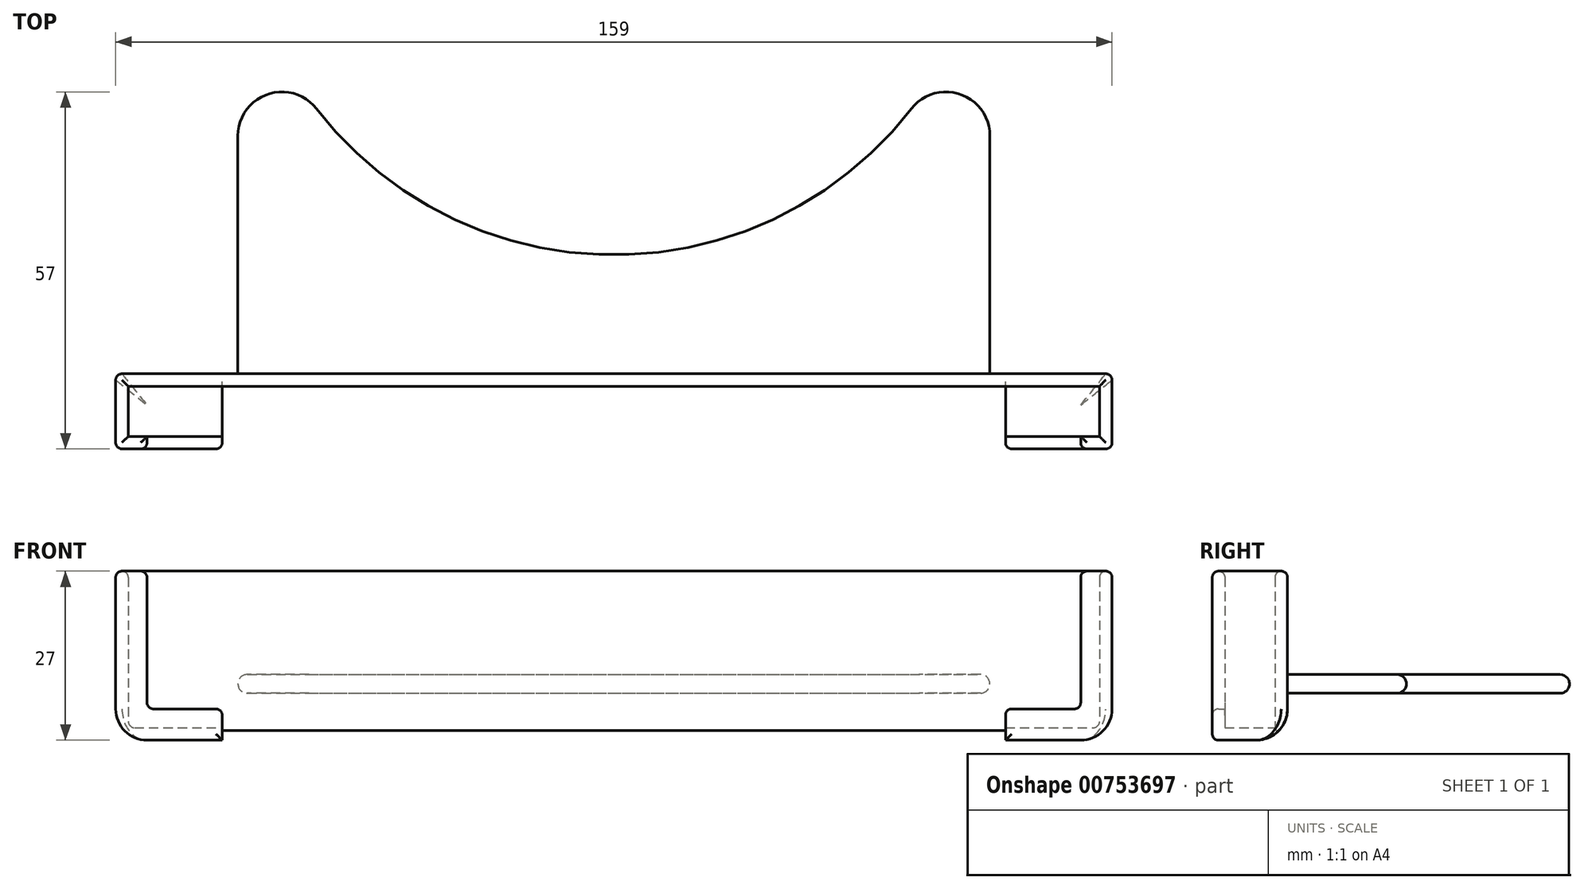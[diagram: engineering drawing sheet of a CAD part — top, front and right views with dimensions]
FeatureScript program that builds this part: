
annotation { "Feature Type Name" : "Feature", "Feature Type Description" : "" }
export const myFeature = defineFeature(function(context is Context, id is Id, definition is map)
    precondition{}
    {
        {
            var Q0;
            Q0=qCreatedBy(makeId("Front.planeOp"),FACE);
            var sketch = newSketch(context, id + "F0", { "sketchPlane" : qUnion([Q0])});
            skLineSegment(sketch, "E0.bottom", {"start": v(-77.5, 19.5) * mm, "end": v(77.5, 19.5) * mm});
            skLineSegment(sketch, "E0.top", {"start": v(-77.5, -5.5) * mm, "end": v(77.5, -5.5) * mm});
            skLineSegment(sketch, "E0.left", {"start": v(-77.5, 19.5) * mm, "end": v(-77.5, -5.5) * mm});
            skLineSegment(sketch, "E0.right", {"start": v(77.5, 19.5) * mm, "end": v(77.5, -5.5) * mm});
            skPoint(sketch, "E1", {"position": v(0, 19.5) * mm});
            skLineSegment(sketch, "E2", {"start": v(-77.5, 19.5) * mm, "end": v(-79.5, 19.5) * mm});
            skLineSegment(sketch, "E3", {"start": v(-79.5, 19.5) * mm, "end": v(-79.5, -7.5) * mm});
            skLineSegment(sketch, "E4", {"start": v(-79.5, -7.5) * mm, "end": v(79.5, -7.5) * mm});
            skLineSegment(sketch, "E5", {"start": v(79.5, -7.5) * mm, "end": v(79.5, 19.5) * mm});
            skLineSegment(sketch, "E6", {"start": v(79.5, 19.5) * mm, "end": v(77.5, 19.5) * mm});
            skLineSegment(sketch, "E7", {"start": v(-62.5, -5.5) * mm, "end": v(-62.5, -7.5) * mm});
            skLineSegment(sketch, "E8", {"start": v(62.5, -5.5) * mm, "end": v(62.5, -7.5) * mm});
            skSolve(sketch);
        }
        {
            var Q0;
            Q0=makeQuery(id+"F0.imprint","IMPRINT",FACE,{"disambiguationData":[TD([[makeQuery(id+"F0.imprint","IMPRINT",EDGE,{"derivedFrom":sQuery(id+"F0.wireOp",EDGE,"E0.bottom")}),-1.0]])]});
            var Q1;
            {var subQ0=sQuery(id+"F0.wireOp",EDGE,"E7");Q1=makeQuery(id+"F0.imprint","IMPRINT",FACE,{"disambiguationData":[TD([[makeQuery(id+"F0.imprint","IMPRINT",EDGE,{"derivedFrom":subQ0}),1.0]])]});}
            extrude(context, id + "F1", {"entities" : qUnion([Q0, Q1]), "depth" : 2 * mm, "offsetDistance" : 25 * mm});
        }
        {
            var Q0;
            {var subQ1=sQuery(id+"F0.wireOp",EDGE,"E0.left");Q0=makeQuery(id+"F0.imprint","IMPRINT",FACE,{"disambiguationData":[TD([[makeQuery(id+"F0.imprint","IMPRINT",EDGE,{"derivedFrom":subQ1}),-1.0]])]});}
            var Q1;
            {var subQ3=sQuery(id+"F0.wireOp",EDGE,"E0.right");Q1=makeQuery(id+"F0.imprint","IMPRINT",FACE,{"disambiguationData":[TD([[makeQuery(id+"F0.imprint","IMPRINT",EDGE,{"derivedFrom":subQ3}),1.0]])]});}
            extrude(context, id + "F2", {"entities" : qUnion([Q0, Q1]), "operationType" : NewBodyOperationType.ADD, "depth" : 10 * mm, "offsetDistance" : 25 * mm});
        }
        {
            var Q0;
            Q0=makeQuery(id+"F2.opExtrude","CAP_FACE",FACE,{"disambiguationData":[OSD([sQuery(id+"F0.wireOp",EDGE,"E0.top"),sQuery(id+"F0.wireOp",EDGE,"E0.left"),sQuery(id+"F0.wireOp",EDGE,"E2"),sQuery(id+"F0.wireOp",EDGE,"E3"),sQuery(id+"F0.wireOp",EDGE,"E4"),sQuery(id+"F0.wireOp",EDGE,"E7")])],"isStart":false});
            var sketch = newSketch(context, id + "F3", { "sketchPlane" : qUnion([Q0])});
            skLineSegment(sketch, "E9.bottom", {"start": v(-79.5, 19.5) * mm, "end": v(-74.5, 19.5) * mm});
            skLineSegment(sketch, "E9.top", {"start": v(-79.5, -7.5) * mm, "end": v(-74.5, -7.5) * mm});
            skLineSegment(sketch, "E9.left", {"start": v(-79.5, 19.5) * mm, "end": v(-79.5, -7.5) * mm});
            skLineSegment(sketch, "E9.right", {"start": v(-74.5, 19.5) * mm, "end": v(-74.5, -2.5) * mm});
            skLineSegment(sketch, "E10.bottom", {"start": v(-74.5, -2.5) * mm, "end": v(-62.5, -2.5) * mm});
            skLineSegment(sketch, "E10.top", {"start": v(-74.5, -7.5) * mm, "end": v(-62.5, -7.5) * mm});
            skLineSegment(sketch, "E10.right", {"start": v(-62.5, -2.5) * mm, "end": v(-62.5, -7.5) * mm});
            skLineSegment(sketch, "E11", {"start": v(0, 71.23) * mm, "end": v(0, -48.1) * mm, "construction": true});
            skLineSegment(sketch, "E12.MirrorCS", {"start": v(74.5, -7.5) * mm, "end": v(62.5, -7.5) * mm});
            skLineSegment(sketch, "E13.MirrorCS", {"start": v(74.5, 19.5) * mm, "end": v(74.5, -2.5) * mm});
            skLineSegment(sketch, "E14.MirrorCS", {"start": v(79.5, 19.5) * mm, "end": v(79.5, -7.5) * mm});
            skLineSegment(sketch, "E15.MirrorCS", {"start": v(62.5, -2.5) * mm, "end": v(62.5, -7.5) * mm});
            skLineSegment(sketch, "E16.MirrorCS", {"start": v(79.5, 19.5) * mm, "end": v(74.5, 19.5) * mm});
            skLineSegment(sketch, "E17.MirrorCS", {"start": v(74.5, -2.5) * mm, "end": v(62.5, -2.5) * mm});
            skLineSegment(sketch, "E18.MirrorCS", {"start": v(79.5, -7.5) * mm, "end": v(74.5, -7.5) * mm});
            skSolve(sketch);
        }
        {
            var Q0;
            Q0 = qSketchRegion(id + "F3", true);
            extrude(context, id + "F4", {"entities" : qUnion([Q0]), "operationType" : NewBodyOperationType.ADD, "depth" : 2 * mm, "offsetDistance" : 25 * mm});
        }
        {
            var Q0;
            Q0=qCreatedBy(makeId("Top.planeOp"),FACE);
            var sketch = newSketch(context, id + "F5", { "sketchPlane" : qUnion([Q0])});
            skLineSegment(sketch, "E19", {"start": v(-60, 0) * mm, "end": v(-60, 38) * mm});
            skLineSegment(sketch, "E20", {"start": v(60, 0) * mm, "end": v(60, 38) * mm});
            skArc(sketch, "E21", {"start": v(-47.46, 42.28) * mm, "mid": v(-55.26, 44.62) * mm, "end": v(-60, 38) * mm});
            skArc(sketch, "E22", {"start": v(60, 38) * mm, "mid": v(55.26, 44.62) * mm, "end": v(47.46, 42.28) * mm});
            skLineSegment(sketch, "E23", {"start": v(0, 0) * mm, "end": v(0, 78.99) * mm, "construction": true});
            skLineSegment(sketch, "E24", {"start": v(-60, 0) * mm, "end": v(60, 0) * mm});
            skPoint(sketch, "E25", {"position": v(-53, 45) * mm});
            skArc(sketch, "E26", {"start": v(-47.46, 42.28) * mm, "mid": v(0, 18.99) * mm, "end": v(47.46, 42.28) * mm});
            skPoint(sketch, "E27", {"position": v(-47.46, 42.28) * mm});
            skPoint(sketch, "E28", {"position": v(47.46, 42.28) * mm});
            skSolve(sketch);
        }
        {
            var Q0;
            Q0 = qSketchRegion(id + "F5", true);
            extrude(context, id + "F6", {"entities" : qUnion([Q0]), "operationType" : NewBodyOperationType.ADD, "depth" : 3 * mm, "offsetDistance" : 25 * mm});
        }
        {
            var Q0;
            Q0=makeQuery(id+"F6.opExtrude","SWEPT_FACE",FACE,{"disambiguationData":[OSD([sQuery(id+"F5.wireOp",EDGE,"E26")])]});
            fillet(context, id + "F7", {"entities" : qUnion([Q0]), "radius" : 1.5 * mm, "tangentPropagation" : true, "allowEdgeOverflow" : false});
        }
        {
            var Q0;
            Q0=makeQuery(id+"F4.boolean.opBoolean","MERGE",EDGE,{"derivedFrom":[makeQuery(id+"F2.opExtrude","SWEPT_EDGE",EDGE,{"disambiguationData":[OSD([sQuery(id+"F0.wireOp",EDGE,"E3"),sQuery(id+"F0.wireOp",EDGE,"E4")])]}),makeQuery(id+"F4.opExtrude","SWEPT_EDGE",EDGE,{"disambiguationData":[OSD([sQuery(id+"F3.wireOp",EDGE,"E9.top"),sQuery(id+"F3.wireOp",EDGE,"E9.left")])]})]});
            var Q1;
            {var subQ0=sQuery(id+"F0.wireOp",EDGE,"E4");Q1=makeQuery(id+"F2.boolean.opBoolean","MERGE",EDGE,{"derivedFrom":[makeQuery(id+"F1.opExtrude","CAP_EDGE",EDGE,{"disambiguationData":[OSD([subQ0])],"isStart":true}),makeQuery(id+"F2.opExtrude","CAP_EDGE",EDGE,{"disambiguationData":[OSD([subQ0]),TDD([makeQuery(id+"F0.imprint","IMPRINT",EDGE,{"disambiguationData":[TD([[makeQuery(id+"F0.imprint","INTERSECT",VERTEX,{"derivedFrom":[subQ0,sQuery(id+"F0.wireOp",EDGE,"E5")]}),1.0]])],"derivedFrom":subQ0})])],"isStart":true}),makeQuery(id+"F2.opExtrude","CAP_EDGE",EDGE,{"disambiguationData":[OSD([subQ0]),TDD([makeQuery(id+"F0.imprint","IMPRINT",EDGE,{"disambiguationData":[TD([[makeQuery(id+"F0.imprint","INTERSECT",VERTEX,{"derivedFrom":[sQuery(id+"F0.wireOp",EDGE,"E3"),subQ0]}),-1.0]])],"derivedFrom":subQ0})])],"isStart":true})]});}
            var Q2;
            Q2=makeQuery(id+"F4.boolean.opBoolean","MERGE",EDGE,{"derivedFrom":[makeQuery(id+"F2.opExtrude","SWEPT_EDGE",EDGE,{"disambiguationData":[OSD([sQuery(id+"F0.wireOp",EDGE,"E4"),sQuery(id+"F0.wireOp",EDGE,"E5")])]}),makeQuery(id+"F4.opExtrude","SWEPT_EDGE",EDGE,{"disambiguationData":[OSD([sQuery(id+"F3.wireOp",EDGE,"E14.MirrorCS"),sQuery(id+"F3.wireOp",EDGE,"E18.MirrorCS")])]})]});
            fillet(context, id + "F8", {"entities" : qUnion([Q0, Q1, Q2]), "tangentPropagation" : true, "radius" : 5 * mm, "defaultsChanged" : false, "vertexSettings" : [], "allowEdgeOverflow" : false});
        }
        {
            var Q0;
            {var subQ0=sQuery(id+"F0.wireOp",EDGE,"E8");var subQ1=sQuery(id+"F0.wireOp",EDGE,"E7");var subQ2=sQuery(id+"F0.wireOp",EDGE,"E4");Q0=makeQuery(id+"F8.opFillet","BLEND_EDGE",EDGE,{"blendedFrom":[makeQuery(id+"F2.boolean.opBoolean","MERGE",EDGE,{"derivedFrom":[makeQuery(id+"F1.opExtrude","CAP_EDGE",EDGE,{"disambiguationData":[OSD([subQ2])],"isStart":true}),makeQuery(id+"F2.opExtrude","CAP_EDGE",EDGE,{"disambiguationData":[OSD([subQ2]),TDD([makeQuery(id+"F0.imprint","IMPRINT",EDGE,{"disambiguationData":[TD([[makeQuery(id+"F0.imprint","INTERSECT",VERTEX,{"derivedFrom":[subQ2,sQuery(id+"F0.wireOp",EDGE,"E5")]}),1.0]])],"derivedFrom":subQ2})])],"isStart":true}),makeQuery(id+"F2.opExtrude","CAP_EDGE",EDGE,{"disambiguationData":[OSD([subQ2]),TDD([makeQuery(id+"F0.imprint","IMPRINT",EDGE,{"disambiguationData":[TD([[makeQuery(id+"F0.imprint","INTERSECT",VERTEX,{"derivedFrom":[sQuery(id+"F0.wireOp",EDGE,"E3"),subQ2]}),-1.0]])],"derivedFrom":subQ2})])],"isStart":true})]}),makeQuery(id+"F1.opExtrude","CAP_FACE",FACE,{"disambiguationData":[OSD([sQuery(id+"F0.wireOp",EDGE,"E0.bottom"),sQuery(id+"F0.wireOp",EDGE,"E0.top"),sQuery(id+"F0.wireOp",EDGE,"E0.left"),sQuery(id+"F0.wireOp",EDGE,"E0.right"),subQ2,subQ1,subQ0])],"isStart":false})],"blendedInto":[makeQuery(id+"F1.opExtrude","CAP_FACE",FACE,{"disambiguationData":[OSD([sQuery(id+"F0.wireOp",EDGE,"E0.bottom"),sQuery(id+"F0.wireOp",EDGE,"E0.top"),sQuery(id+"F0.wireOp",EDGE,"E0.left"),sQuery(id+"F0.wireOp",EDGE,"E0.right"),subQ2,subQ1,subQ0])],"isStart":false})]});}
            fillet(context, id + "F9", {"entities" : qUnion([Q0]), "tangentPropagation" : true, "radius" : .43 * mm, "defaultsChanged" : true, "vertexSettings" : [], "allowEdgeOverflow" : false});
        }
        {
            var Q0;
            Q0=makeQuery(id+"F4.opExtrude","CAP_FACE",FACE,{"disambiguationData":[OSD([sQuery(id+"F3.wireOp",EDGE,"E9.bottom"),sQuery(id+"F3.wireOp",EDGE,"E9.top"),sQuery(id+"F3.wireOp",EDGE,"E9.left"),sQuery(id+"F3.wireOp",EDGE,"E9.right"),sQuery(id+"F3.wireOp",EDGE,"E10.bottom"),sQuery(id+"F3.wireOp",EDGE,"E10.top"),sQuery(id+"F3.wireOp",EDGE,"E10.right")])],"isStart":false});
            var Q1;
            Q1=makeQuery(id+"F4.opExtrude","CAP_FACE",FACE,{"disambiguationData":[OSD([sQuery(id+"F3.wireOp",EDGE,"E12.MirrorCS"),sQuery(id+"F3.wireOp",EDGE,"E13.MirrorCS"),sQuery(id+"F3.wireOp",EDGE,"E14.MirrorCS"),sQuery(id+"F3.wireOp",EDGE,"E15.MirrorCS"),sQuery(id+"F3.wireOp",EDGE,"E16.MirrorCS"),sQuery(id+"F3.wireOp",EDGE,"E17.MirrorCS"),sQuery(id+"F3.wireOp",EDGE,"E18.MirrorCS")])],"isStart":false});
            var Q2;
            Q2=makeQuery(id+"F2.opExtrude","CAP_EDGE",EDGE,{"disambiguationData":[OSD([sQuery(id+"F0.wireOp",EDGE,"E3")])],"isStart":true});
            var Q3;
            Q3=makeQuery(id+"F2.opExtrude","CAP_EDGE",EDGE,{"disambiguationData":[OSD([sQuery(id+"F0.wireOp",EDGE,"E5")])],"isStart":true});
            var Q4;
            Q4=makeQuery(id+"F4.boolean.opBoolean","MERGE",FACE,{"derivedFrom":[makeQuery(id+"F2.boolean.opBoolean","MERGE",FACE,{"derivedFrom":[makeQuery(id+"F1.opExtrude","SWEPT_FACE",FACE,{"disambiguationData":[OSD([sQuery(id+"F0.wireOp",EDGE,"E0.bottom")])]}),makeQuery(id+"F2.opExtrude","SWEPT_FACE",FACE,{"disambiguationData":[OSD([sQuery(id+"F0.wireOp",EDGE,"E2")])]}),makeQuery(id+"F2.opExtrude","SWEPT_FACE",FACE,{"disambiguationData":[OSD([sQuery(id+"F0.wireOp",EDGE,"E6")])]})]}),makeQuery(id+"F4.opExtrude","SWEPT_FACE",FACE,{"disambiguationData":[OSD([sQuery(id+"F3.wireOp",EDGE,"E9.bottom")])]}),makeQuery(id+"F4.opExtrude","SWEPT_FACE",FACE,{"disambiguationData":[OSD([sQuery(id+"F3.wireOp",EDGE,"E16.MirrorCS")])]})]});
            var Q5;
            Q5=makeQuery(id+"F4.opExtrude","SWEPT_EDGE",EDGE,{"disambiguationData":[OSD([sQuery(id+"F3.wireOp",EDGE,"E10.bottom"),sQuery(id+"F3.wireOp",EDGE,"E10.right")])]});
            var Q6;
            Q6=makeQuery(id+"F4.opExtrude","SWEPT_EDGE",EDGE,{"disambiguationData":[OSD([sQuery(id+"F3.wireOp",EDGE,"E15.MirrorCS"),sQuery(id+"F3.wireOp",EDGE,"E17.MirrorCS")])]});
            var Q7;
            Q7=makeQuery(id+"F4.opExtrude","SWEPT_EDGE",EDGE,{"disambiguationData":[OSD([sQuery(id+"F3.wireOp",EDGE,"E9.right"),sQuery(id+"F3.wireOp",EDGE,"E10.bottom")])]});
            var Q8;
            Q8=makeQuery(id+"F4.opExtrude","SWEPT_EDGE",EDGE,{"disambiguationData":[OSD([sQuery(id+"F3.wireOp",EDGE,"E13.MirrorCS"),sQuery(id+"F3.wireOp",EDGE,"E17.MirrorCS")])]});
            var Q9;
            Q9=makeQuery(id+"F2.opExtrude","SWEPT_EDGE",EDGE,{"disambiguationData":[OSD([sQuery(id+"F0.wireOp",EDGE,"E0.top"),sQuery(id+"F0.wireOp",EDGE,"E0.right")])]});
            var Q10;
            Q10=makeQuery(id+"F2.opExtrude","SWEPT_EDGE",EDGE,{"disambiguationData":[OSD([sQuery(id+"F0.wireOp",EDGE,"E0.top"),sQuery(id+"F0.wireOp",EDGE,"E0.left")])]});
            var Q11;
            {var subQ0=sQuery(id+"F0.wireOp",EDGE,"E0.top");Q11=makeQuery(id+"F1.opExtrude","CAP_EDGE",EDGE,{"disambiguationData":[OSD([subQ0]),TDD([makeQuery(id+"F0.imprint","IMPRINT",EDGE,{"disambiguationData":[TD([[makeQuery(id+"F0.imprint","INTERSECT",VERTEX,{"derivedFrom":[subQ0,sQuery(id+"F0.wireOp",EDGE,"E7")]}),1.0]])],"derivedFrom":subQ0})])],"isStart":false});}
            var Q12;
            {var subQ0=sQuery(id+"F0.wireOp",EDGE,"E0.top");Q12=makeQuery(id+"F1.opExtrude","CAP_EDGE",EDGE,{"disambiguationData":[OSD([subQ0]),TDD([makeQuery(id+"F0.imprint","IMPRINT",EDGE,{"disambiguationData":[TD([[makeQuery(id+"F0.imprint","INTERSECT",VERTEX,{"derivedFrom":[subQ0,sQuery(id+"F0.wireOp",EDGE,"E0.right")]}),1.0]])],"derivedFrom":subQ0})])],"isStart":false});}
            fillet(context, id + "F10", {"entities" : qUnion([Q0, Q1, Q2, Q3, Q4, Q5, Q6, Q7, Q8, Q9, Q10, Q11, Q12]), "tangentPropagation" : true, "radius" : 1 * mm, "defaultsChanged" : false, "vertexSettings" : [], "allowEdgeOverflow" : false});
        }
    });
